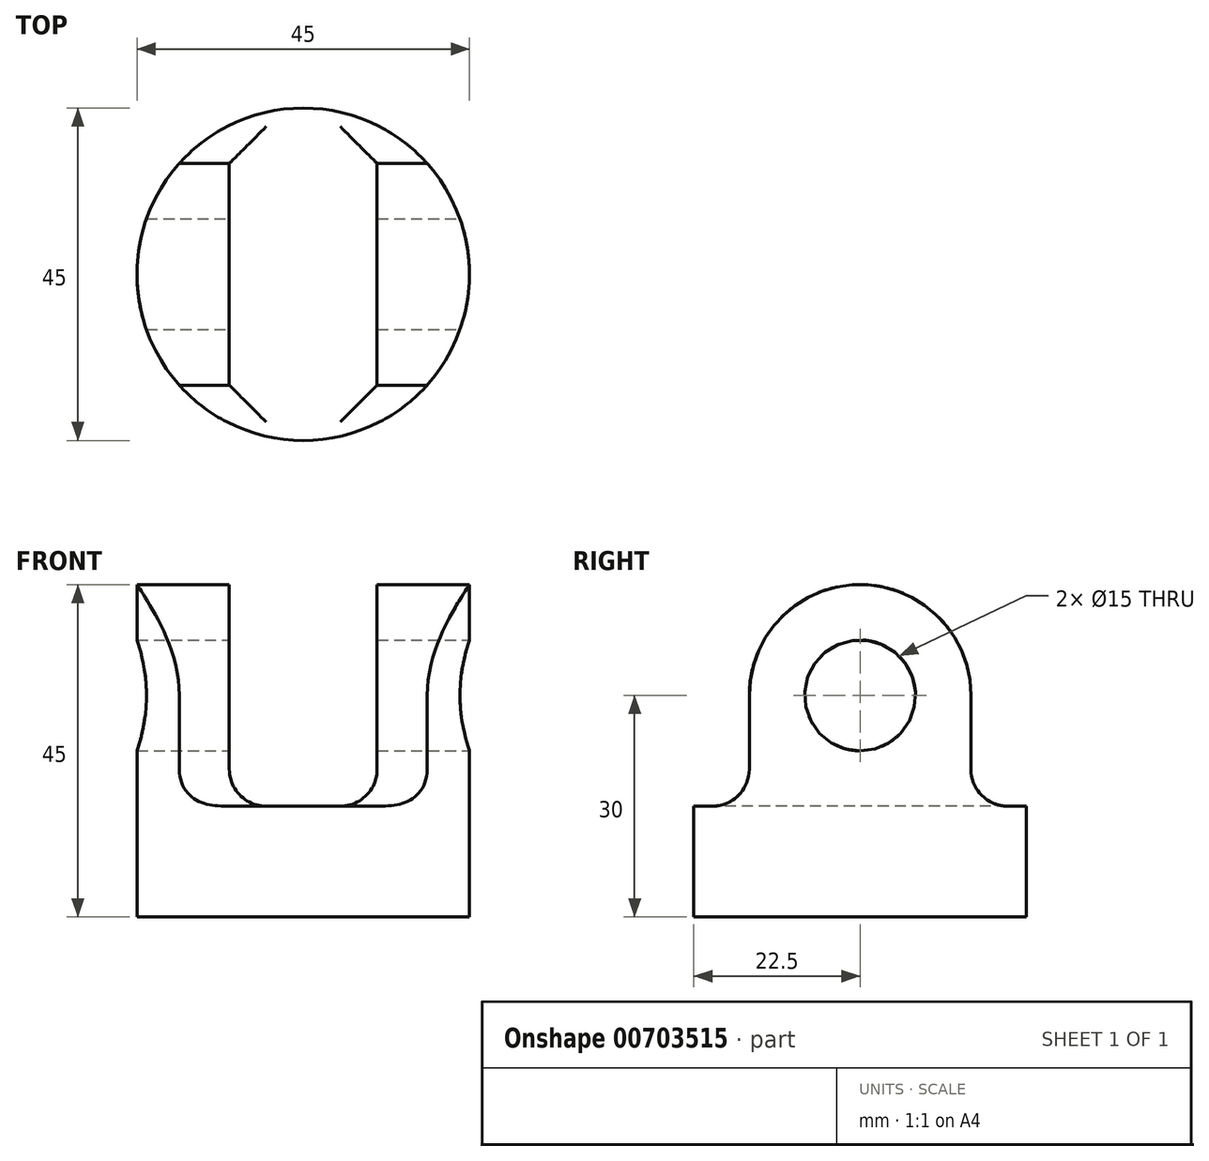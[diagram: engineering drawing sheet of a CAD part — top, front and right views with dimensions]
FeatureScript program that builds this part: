
annotation { "Feature Type Name" : "Feature", "Feature Type Description" : "" }
export const myFeature = defineFeature(function(context is Context, id is Id, definition is map)
    precondition{}
    {
        {
            var Q0;
            Q0=qCreatedBy(makeId("Top.planeOp"),FACE);
            var sketch = newSketch(context, id + "F0", { "sketchPlane" : qUnion([Q0])});
            skCircle(sketch, "E0", {"center": v(0, 0) * mm, "radius": 22.5 * mm});
            skSolve(sketch);
        }
        {
            var Q0;
            Q0=makeQuery(id+"F0.imprint","IMPRINT",FACE,{"disambiguationData":[TD([[makeQuery(id+"F0.imprint","IMPRINT",EDGE,{"derivedFrom":sQuery(id+"F0.wireOp",EDGE,"E0")}),1.0]])]});
            extrude(context, id + "F1", {"entities" : qUnion([Q0]), "depth" : 45 * mm, "offsetDistance" : 25 * mm});
        }
        {
            var Q0;
            Q0=qCreatedBy(makeId("Right.planeOp"),FACE);
            cPlane(context, id + "F2", {"entities" : qUnion([Q0]), "cplaneType" : CPlaneType.OFFSET, "offset" : 22.5 * mm, "width" : 150 * mm, "height" : 150 * mm});
        }
        {
            var Q0;
            Q0=qCreatedBy(id+"F2.planeOp",FACE);
            var sketch = newSketch(context, id + "F3", { "sketchPlane" : qUnion([Q0])});
            skLineSegment(sketch, "E1.0", {"start": v(-22.5, 45) * mm, "end": v(22.5, 45) * mm});
            skLineSegment(sketch, "E2", {"start": v(-22.5, 15) * mm, "end": v(-22.5, 45) * mm});
            skLineSegment(sketch, "E3", {"start": v(22.5, 45) * mm, "end": v(22.5, 15) * mm});
            skArc(sketch, "E4", {"start": v(15, 30) * mm, "mid": v(0, 45) * mm, "end": v(-15, 30) * mm});
            skCircle(sketch, "E5", {"center": v(0, 30) * mm, "radius": 7.5 * mm});
            skLineSegment(sketch, "E6", {"start": v(-15, 30) * mm, "end": v(-15, 15) * mm});
            skLineSegment(sketch, "E7", {"start": v(-15, 15) * mm, "end": v(-22.5, 15) * mm});
            skLineSegment(sketch, "E8", {"start": v(0, 30) * mm, "end": v(0, 0) * mm, "construction": true});
            skLineSegment(sketch, "E9.MirrorCS", {"start": v(15, 30) * mm, "end": v(15, 15) * mm});
            skLineSegment(sketch, "E10.MirrorCS", {"start": v(15, 15) * mm, "end": v(22.5, 15) * mm});
            skSolve(sketch);
        }
        {
            var Q0;
            Q0 = qSketchRegion(id + "F3", true);
            extrude(context, id + "F4", {"entities" : qUnion([Q0]), "operationType" : NewBodyOperationType.REMOVE, "endBound" : BoundingType.THROUGH_ALL, "oppositeDirection" : true, "depth" : 25 * mm, "offsetDistance" : 25 * mm});
        }
        {
            var Q0;
            Q0=makeQuery(id+"F4.boolean.opBoolean","COPY",FACE,{"derivedFrom":makeQuery(id+"F4.opExtrude","SWEPT_FACE",FACE,{"disambiguationData":[OSD([sQuery(id+"F3.wireOp",EDGE,"E6")])]})});
            var sketch = newSketch(context, id + "F5", { "sketchPlane" : qUnion([Q0])});
            skLineSegment(sketch, "E11.bottom", {"start": v(-10, 15) * mm, "end": v(10, 15) * mm});
            skLineSegment(sketch, "E11.top", {"start": v(-10, 47.58) * mm, "end": v(10, 47.58) * mm});
            skLineSegment(sketch, "E11.left", {"start": v(-10, 15) * mm, "end": v(-10, 47.58) * mm});
            skLineSegment(sketch, "E11.right", {"start": v(10, 15) * mm, "end": v(10, 47.58) * mm});
            skLineSegment(sketch, "E12", {"start": v(0, 6.58) * mm, "end": v(0, 63.57) * mm, "construction": true});
            skLineSegment(sketch, "E13.0.1", {"start": v(16.77, 30) * mm, "end": v(-16.77, 30) * mm});
            skFitSpline(sketch, "E13.0.2", {"points": [v(-16.77, 30) * mm, v(-16.77, 31.03) * mm, v(-16.89, 32.28) * mm, v(-17.18, 33.74) * mm, v(-17.4, 34.7) * mm, v(-17.75, 35.86) * mm, v(-18.22, 37.16) * mm, v(-18.74, 38.4) * mm, v(-19.29, 39.54) * mm, v(-19.83, 40.6) * mm, v(-20.37, 41.56) * mm, v(-20.87, 42.43) * mm, v(-21.33, 43.18) * mm, v(-21.73, 43.82) * mm, v(-22.07, 44.34) * mm, v(-22.31, 44.72) * mm, v(-22.46, 44.95) * mm, v(-22.5, 45) * mm, v(-22.5, 45) * mm]});
            skLineSegment(sketch, "E13.0.3", {"start": v(-16.77, 30) * mm, "end": v(16.77, 30) * mm});
            skSolve(sketch);
        }
        {
            var Q0;
            {var subQ0=sQuery(id+"F5.wireOp",EDGE,"E11.top");Q0=makeQuery(id+"F5.imprint","IMPRINT",FACE,{"disambiguationData":[TD([[makeQuery(id+"F5.imprint","IMPRINT",EDGE,{"derivedFrom":subQ0}),-1.0]])]});}
            var Q1;
            {var subQ0=sQuery(id+"F5.wireOp",EDGE,"E11.bottom");Q1=makeQuery(id+"F5.imprint","IMPRINT",FACE,{"disambiguationData":[TD([[makeQuery(id+"F5.imprint","IMPRINT",EDGE,{"derivedFrom":subQ0}),1.0]])]});}
            extrude(context, id + "F6", {"entities" : qUnion([Q0, Q1]), "operationType" : NewBodyOperationType.REMOVE, "endBound" : BoundingType.THROUGH_ALL, "oppositeDirection" : true, "depth" : 25 * mm, "offsetDistance" : 25 * mm});
        }
        {
            var Q0;
            Q0=makeQuery(id+"F6.boolean.opBoolean","COPY",EDGE,{"derivedFrom":makeQuery(id+"F6.opExtrude","SWEPT_EDGE",EDGE,{"disambiguationData":[OSD([sQuery(id+"F3.wireOp",EDGE,"E6"),sQuery(id+"F3.wireOp",EDGE,"E7"),sQuery(id+"F5.wireOp",EDGE,"E11.bottom"),sQuery(id+"F5.wireOp",EDGE,"E11.right")])]})});
            var Q1;
            {var subQ0=sQuery(id+"F3.wireOp",EDGE,"E7");var subQ1=sQuery(id+"F3.wireOp",EDGE,"E6");Q1=makeQuery(id+"F6.boolean.opBoolean","SPLIT",EDGE,{"disambiguationData":[TD([makeQuery(id+"F6.opExtrude","SWEPT_FACE",FACE,{"disambiguationData":[OSD([sQuery(id+"F5.wireOp",EDGE,"E11.right")])]})])],"derivedFrom":makeQuery(id+"F4.boolean.opBoolean","COPY",EDGE,{"derivedFrom":makeQuery(id+"F4.opExtrude","SWEPT_EDGE",EDGE,{"disambiguationData":[OSD([subQ1,subQ0])]})})});}
            var Q2;
            {var subQ0=sQuery(id+"F3.wireOp",EDGE,"E7");var subQ1=sQuery(id+"F3.wireOp",EDGE,"E6");Q2=makeQuery(id+"F6.boolean.opBoolean","SPLIT",EDGE,{"disambiguationData":[TD([makeQuery(id+"F6.opExtrude","SWEPT_FACE",FACE,{"disambiguationData":[OSD([sQuery(id+"F5.wireOp",EDGE,"E11.left")])]})])],"derivedFrom":makeQuery(id+"F4.boolean.opBoolean","COPY",EDGE,{"derivedFrom":makeQuery(id+"F4.opExtrude","SWEPT_EDGE",EDGE,{"disambiguationData":[OSD([subQ1,subQ0])]})})});}
            var Q3;
            Q3=makeQuery(id+"F6.boolean.opBoolean","COPY",EDGE,{"derivedFrom":makeQuery(id+"F6.opExtrude","SWEPT_EDGE",EDGE,{"disambiguationData":[OSD([sQuery(id+"F3.wireOp",EDGE,"E6"),sQuery(id+"F3.wireOp",EDGE,"E7"),sQuery(id+"F5.wireOp",EDGE,"E11.bottom"),sQuery(id+"F5.wireOp",EDGE,"E11.left")])]})});
            var Q4;
            {var subQ0=sQuery(id+"F3.wireOp",EDGE,"E9.MirrorCS");var subQ1=sQuery(id+"F3.wireOp",EDGE,"E10.MirrorCS");Q4=makeQuery(id+"F6.boolean.opBoolean","SPLIT",EDGE,{"disambiguationData":[TD([makeQuery(id+"F6.opExtrude","SWEPT_FACE",FACE,{"disambiguationData":[OSD([sQuery(id+"F5.wireOp",EDGE,"E11.right")])]})])],"derivedFrom":makeQuery(id+"F4.boolean.opBoolean","COPY",EDGE,{"derivedFrom":makeQuery(id+"F4.opExtrude","SWEPT_EDGE",EDGE,{"disambiguationData":[OSD([subQ0,subQ1])]})})});}
            var Q5;
            {var subQ0=sQuery(id+"F3.wireOp",EDGE,"E9.MirrorCS");var subQ1=sQuery(id+"F3.wireOp",EDGE,"E10.MirrorCS");Q5=makeQuery(id+"F6.boolean.opBoolean","SPLIT",EDGE,{"disambiguationData":[TD([makeQuery(id+"F6.opExtrude","SWEPT_FACE",FACE,{"disambiguationData":[OSD([sQuery(id+"F5.wireOp",EDGE,"E11.left")])]})])],"derivedFrom":makeQuery(id+"F4.boolean.opBoolean","COPY",EDGE,{"derivedFrom":makeQuery(id+"F4.opExtrude","SWEPT_EDGE",EDGE,{"disambiguationData":[OSD([subQ0,subQ1])]})})});}
            fillet(context, id + "F7", {"entities" : qUnion([Q0, Q1, Q2, Q3, Q4, Q5]), "radius" : 5 * mm, "tangentPropagation" : true, "allowEdgeOverflow" : false});
        }
    });
